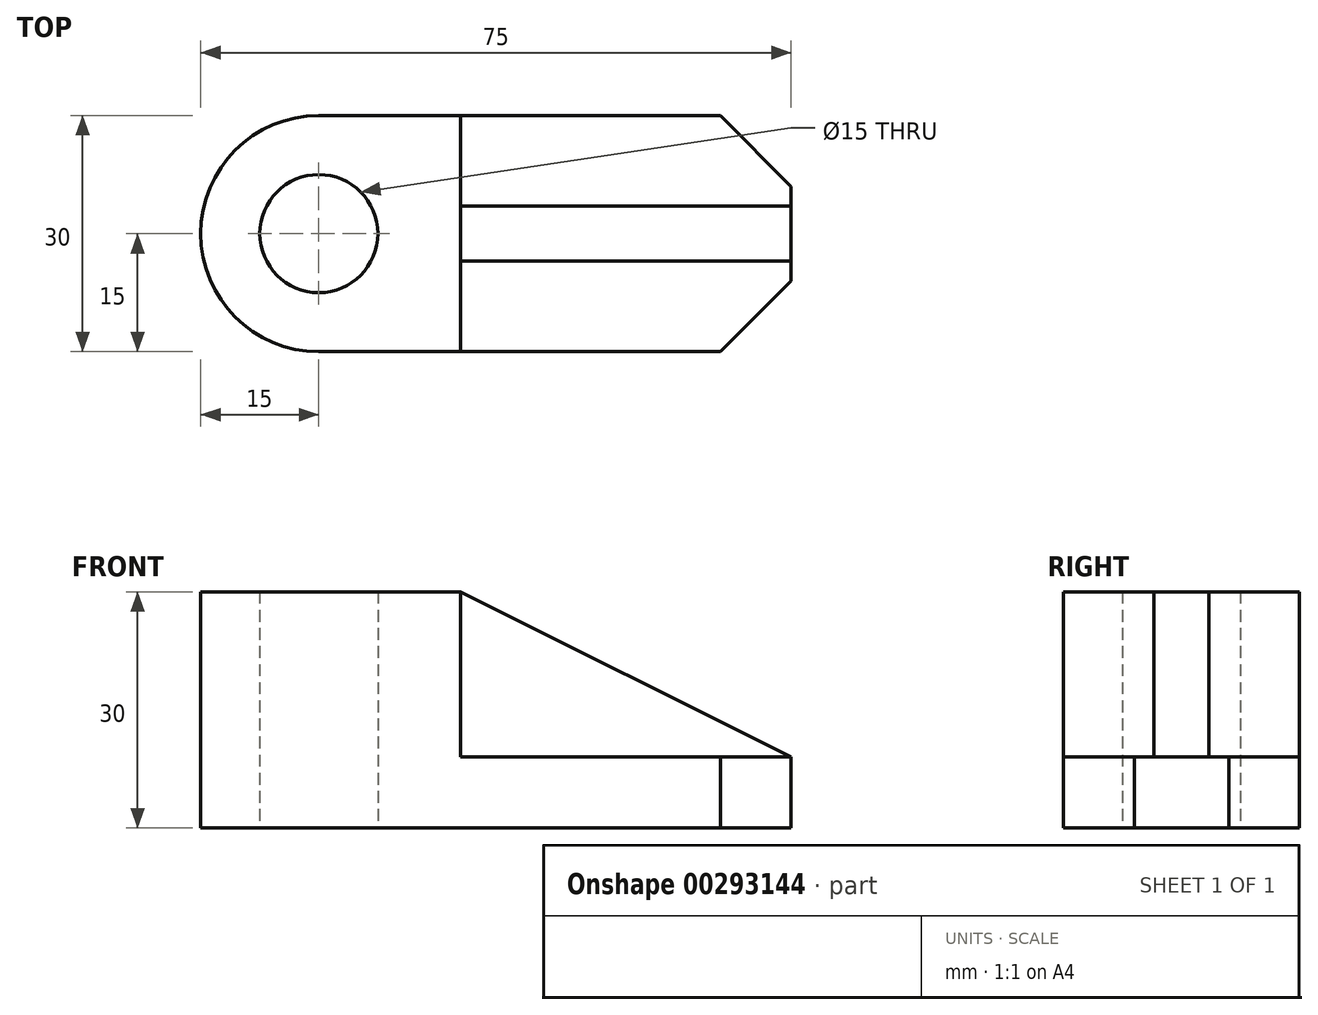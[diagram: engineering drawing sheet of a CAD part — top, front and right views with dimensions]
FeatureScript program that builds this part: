
annotation { "Feature Type Name" : "Feature", "Feature Type Description" : "" }
export const myFeature = defineFeature(function(context is Context, id is Id, definition is map)
    precondition{}
    {
        {
            var Q0;
            Q0=qCreatedBy(makeId("Top.planeOp"),FACE);
            var sketch = newSketch(context, id + "F0", { "sketchPlane" : qUnion([Q0])});
            skLineSegment(sketch, "E0", {"start": v(0, 30) * mm, "end": v(60, 30) * mm});
            skLineSegment(sketch, "E1", {"start": v(60, 30) * mm, "end": v(60, 0) * mm});
            skLineSegment(sketch, "E2", {"start": v(60, 0) * mm, "end": v(0, 0) * mm});
            skArc(sketch, "E3", {"start": v(0, 30) * mm, "mid": v(-15, 15) * mm, "end": v(0, 0) * mm});
            skCircle(sketch, "E4", {"center": v(0, 15) * mm, "radius": 7.5 * mm});
            skSolve(sketch);
        }
        {
            var Q0;
            Q0 = qSketchRegion(id + "F0", true);
            extrude(context, id + "F1", {"entities" : qUnion([Q0]), "depth" : 30 * mm});
        }
        {
            var Q0;
            Q0=makeQuery(id+"F1.opExtrude","SWEPT_FACE",FACE,{"disambiguationData":[OSD([sQuery(id+"F0.wireOp",EDGE,"E2")])]});
            var sketch = newSketch(context, id + "F2", { "sketchPlane" : qUnion([Q0])});
            skLineSegment(sketch, "E5", {"start": v(0, 30) * mm, "end": v(0, 0) * mm, "construction": true});
            skLineSegment(sketch, "E6", {"start": v(18, 30) * mm, "end": v(18, 9) * mm});
            skLineSegment(sketch, "E7", {"start": v(18, 9) * mm, "end": v(60, 9) * mm});
            skPoint(sketch, "E8.orphan", {"position": v(18, 0) * mm});
            skLineSegment(sketch, "E9", {"start": v(18, 30) * mm, "end": v(60, 30) * mm});
            skLineSegment(sketch, "E10", {"start": v(60, 30) * mm, "end": v(60, 9) * mm});
            skSolve(sketch);
        }
        {
            var Q0;
            Q0 = qSketchRegion(id + "F2", true);
            extrude(context, id + "F3", {"entities" : qUnion([Q0]), "operationType" : NewBodyOperationType.REMOVE, "endBound" : BoundingType.THROUGH_ALL, "oppositeDirection" : true, "depth" : 25 * mm});
        }
        {
            var Q0;
            Q0=makeQuery(id+"F1.opExtrude","SWEPT_FACE",FACE,{"disambiguationData":[OSD([sQuery(id+"F0.wireOp",EDGE,"E2")])]});
            var sketch = newSketch(context, id + "F4", { "sketchPlane" : qUnion([Q0])});
            skLineSegment(sketch, "E11", {"start": v(18, 30) * mm, "end": v(18, 9) * mm});
            skLineSegment(sketch, "E12", {"start": v(18, 9) * mm, "end": v(60, 9) * mm});
            skLineSegment(sketch, "E13", {"start": v(60, 9) * mm, "end": v(18, 30) * mm});
            skSolve(sketch);
        }
        {
            var Q0;
            Q0 = qSketchRegion(id + "F4", true);
            extrude(context, id + "F5", {"entities" : qUnion([Q0]), "operationType" : NewBodyOperationType.ADD, "oppositeDirection" : true, "depth" : 18.5 * mm});
        }
        {
            var Q0;
            Q0=makeQuery(id+"F5.boolean.opBoolean","MERGE",FACE,{"derivedFrom":[makeQuery(id+"F1.opExtrude","SWEPT_FACE",FACE,{"disambiguationData":[OSD([sQuery(id+"F0.wireOp",EDGE,"E2")])]}),makeQuery(id+"F5.opExtrude","CAP_FACE",FACE,{"disambiguationData":[OSD([sQuery(id+"F4.wireOp",EDGE,"E11"),sQuery(id+"F4.wireOp",EDGE,"E12"),sQuery(id+"F4.wireOp",EDGE,"E13")])],"isStart":true})]});
            var sketch = newSketch(context, id + "F6", { "sketchPlane" : qUnion([Q0])});
            skLineSegment(sketch, "E14", {"start": v(60, 9) * mm, "end": v(18, 9) * mm});
            skLineSegment(sketch, "E15", {"start": v(18, 9) * mm, "end": v(18, 30) * mm});
            skLineSegment(sketch, "E16", {"start": v(18, 30) * mm, "end": v(60, 9) * mm});
            skSolve(sketch);
        }
        {
            var Q0;
            Q0 = qSketchRegion(id + "F6", true);
            extrude(context, id + "F7", {"entities" : qUnion([Q0]), "operationType" : NewBodyOperationType.REMOVE, "oppositeDirection" : true, "depth" : 11.5 * mm});
        }
        {
            var Q0;
            Q0=makeQuery(id+"F1.opExtrude","SWEPT_EDGE",EDGE,{"disambiguationData":[OSD([sQuery(id+"F0.wireOp",EDGE,"E1"),sQuery(id+"F0.wireOp",EDGE,"E2")])]});
            var Q1;
            Q1=makeQuery(id+"F1.opExtrude","SWEPT_EDGE",EDGE,{"disambiguationData":[OSD([sQuery(id+"F0.wireOp",EDGE,"E0"),sQuery(id+"F0.wireOp",EDGE,"E1")])]});
            chamfer(context, id + "F8", {"entities" : qUnion([Q0, Q1]), "width" : 9 * mm, "tangentPropagation" : true});
        }
    });
